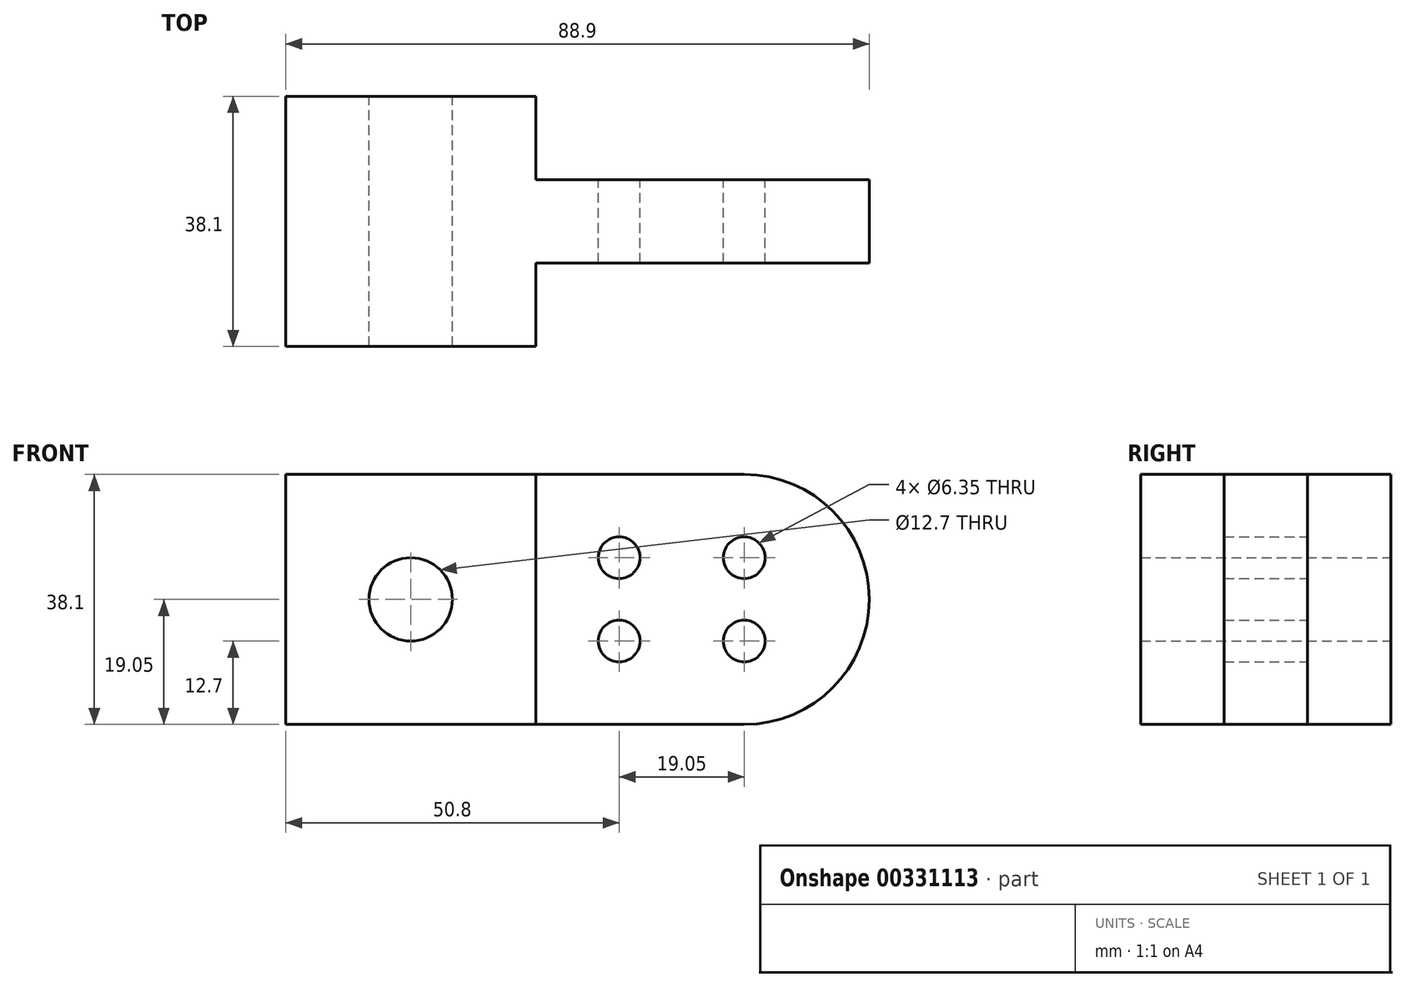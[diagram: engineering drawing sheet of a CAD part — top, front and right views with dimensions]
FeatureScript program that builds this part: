
annotation { "Feature Type Name" : "Feature", "Feature Type Description" : "" }
export const myFeature = defineFeature(function(context is Context, id is Id, definition is map)
    precondition{}
    {
        {
            var Q0;
            Q0=qCreatedBy(makeId("Front.planeOp"),FACE);
            var sketch = newSketch(context, id + "F0", { "sketchPlane" : qUnion([Q0])});
            skLineSegment(sketch, "E0.bottom", {"start": v(0, 0) * mm, "end": v(38.1, 0) * mm});
            skLineSegment(sketch, "E0.top", {"start": v(0, 38.1) * mm, "end": v(38.1, 38.1) * mm});
            skLineSegment(sketch, "E0.left", {"start": v(0, 0) * mm, "end": v(0, 38.1) * mm});
            skLineSegment(sketch, "E0.right", {"start": v(38.1, 0) * mm, "end": v(38.1, 38.1) * mm});
            skCircle(sketch, "E1", {"center": v(19.05, 19.05) * mm, "radius": 6.35 * mm});
            skLineSegment(sketch, "E2", {"start": v(38.1, 38.1) * mm, "end": v(69.85, 38.1) * mm});
            skArc(sketch, "E3", {"start": v(69.85, 0) * mm, "mid": v(88.9, 19.05) * mm, "end": v(69.85, 38.1) * mm});
            skLineSegment(sketch, "E4", {"start": v(69.85, 0) * mm, "end": v(38.1, 0) * mm});
            skLineSegment(sketch, "E5", {"start": v(69.85, 38.1) * mm, "end": v(69.85, 0) * mm, "construction": true});
            skLineSegment(sketch, "E6.bottom", {"start": v(69.85, 25.4) * mm, "end": v(50.8, 25.4) * mm, "construction": true});
            skLineSegment(sketch, "E6.top", {"start": v(69.85, 12.7) * mm, "end": v(50.8, 12.7) * mm, "construction": true});
            skLineSegment(sketch, "E6.left", {"start": v(69.85, 25.4) * mm, "end": v(69.85, 12.7) * mm, "construction": true});
            skLineSegment(sketch, "E6.right", {"start": v(50.8, 25.4) * mm, "end": v(50.8, 12.7) * mm, "construction": true});
            skCircle(sketch, "E7", {"center": v(50.8, 25.4) * mm, "radius": 3.18 * mm});
            skCircle(sketch, "E8", {"center": v(69.85, 25.4) * mm, "radius": 3.18 * mm});
            skCircle(sketch, "E9", {"center": v(50.8, 12.7) * mm, "radius": 3.18 * mm});
            skCircle(sketch, "E10", {"center": v(69.85, 12.7) * mm, "radius": 3.18 * mm});
            skSolve(sketch);
        }
        {
            var Q0;
            Q0=makeQuery(id+"F0.imprint","IMPRINT",FACE,{"disambiguationData":[TD([[makeQuery(id+"F0.imprint","IMPRINT",EDGE,{"derivedFrom":sQuery(id+"F0.wireOp",EDGE,"E0.bottom")}),1.0]])]});
            extrude(context, id + "F1", {"entities" : qUnion([Q0]), "endBound" : BoundingType.SYMMETRIC, "depth" : 38.1 * mm});
        }
        {
            var Q0;
            Q0=makeQuery(id+"F0.imprint","IMPRINT",FACE,{"disambiguationData":[TD([[makeQuery(id+"F0.imprint","IMPRINT",EDGE,{"derivedFrom":sQuery(id+"F0.wireOp",EDGE,"E0.right")}),-1.0]])]});
            extrude(context, id + "F2", {"entities" : qUnion([Q0]), "operationType" : NewBodyOperationType.ADD, "endBound" : BoundingType.SYMMETRIC, "depth" : 12.7 * mm});
        }
    });
